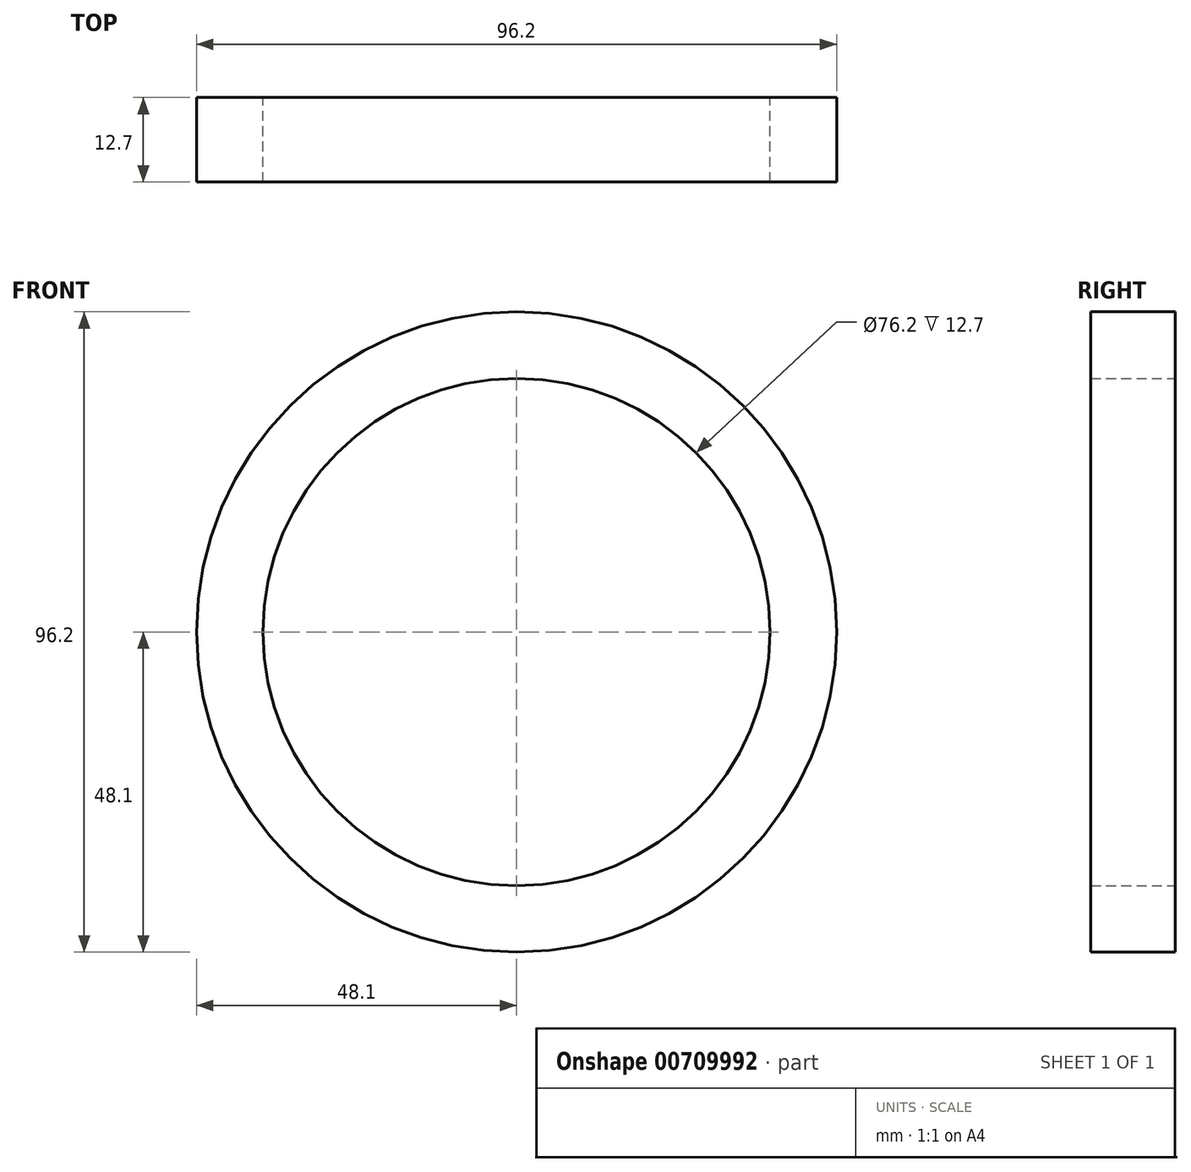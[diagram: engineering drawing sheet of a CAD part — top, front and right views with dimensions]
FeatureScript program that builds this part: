
annotation { "Feature Type Name" : "Feature", "Feature Type Description" : "" }
export const myFeature = defineFeature(function(context is Context, id is Id, definition is map)
    precondition{}
    {
        {
            var Q0;
            Q0=qCreatedBy(makeId("Front.planeOp"),FACE);
            var sketch = newSketch(context, id + "F0", { "sketchPlane" : qUnion([Q0])});
            skCircle(sketch, "E0", {"center": v(0, 0) * mm, "radius": 48.1 * mm});
            skCircle(sketch, "E1", {"center": v(0, 0) * mm, "radius": 38.1 * mm});
            skLineSegment(sketch, "E2", {"start": v(48.1, -55.23) * mm, "end": v(48.1, -55.23) * mm});
            skSolve(sketch);
        }
        {
            var Q0;
            Q0 = qSketchRegion(id + "F0", true);
            extrude(context, id + "F1", {"entities" : qUnion([Q0]), "depth" : 12.7 * mm, "offsetDistance" : 25.4 * mm});
        }
    });
